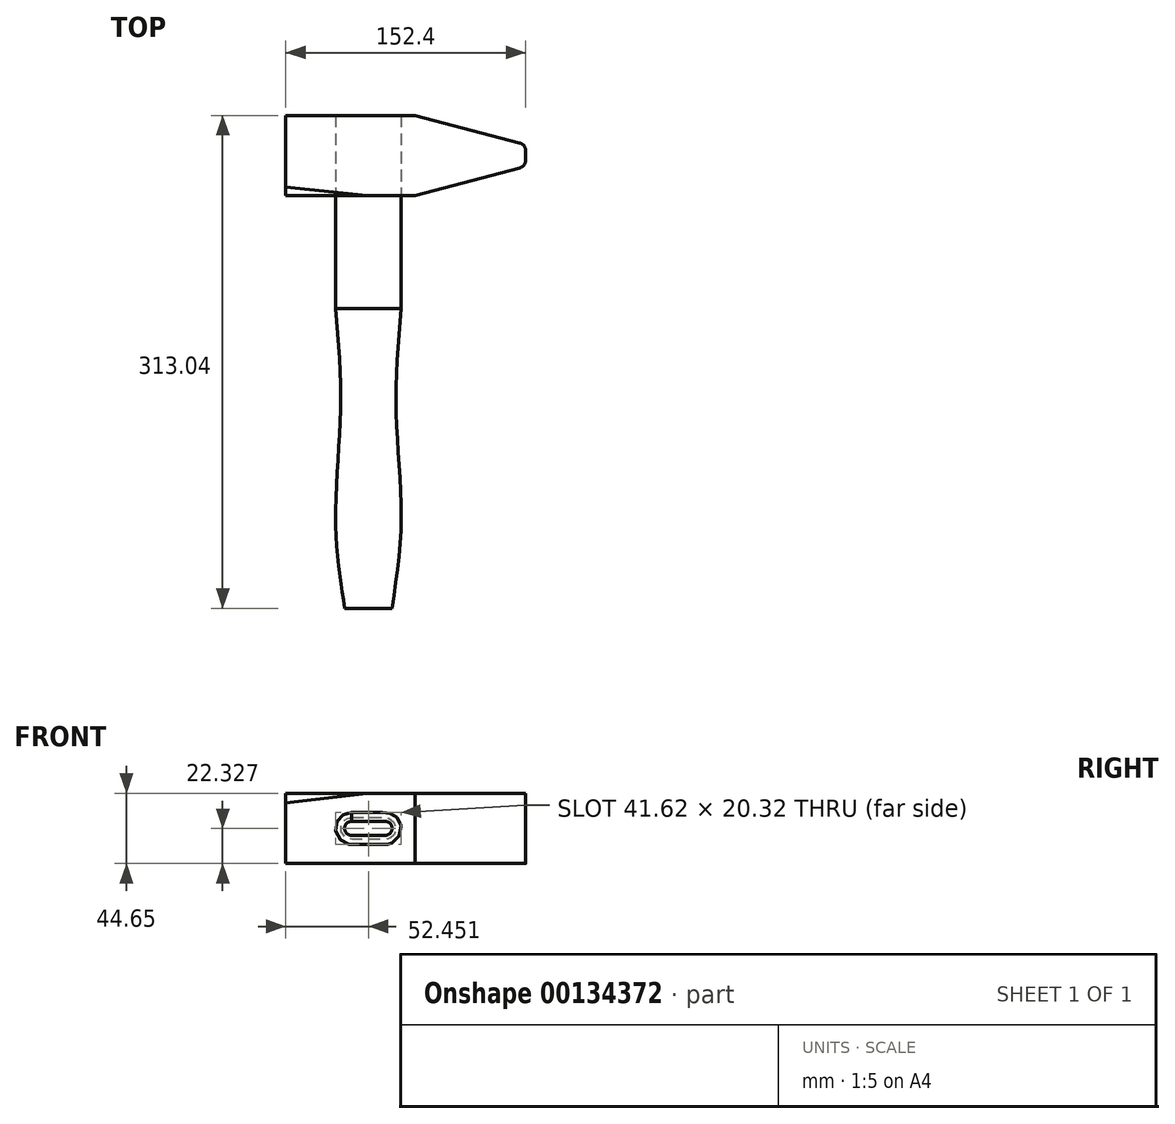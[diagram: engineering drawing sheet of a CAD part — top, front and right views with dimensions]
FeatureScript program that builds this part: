
annotation { "Feature Type Name" : "Feature", "Feature Type Description" : "" }
export const myFeature = defineFeature(function(context is Context, id is Id, definition is map)
    precondition{}
    {
        {
            var Q0;
            Q0=qCreatedBy(makeId("Top.planeOp"),FACE);
            var sketch = newSketch(context, id + "F0", { "sketchPlane" : qUnion([Q0])});
            skLineSegment(sketch, "E0", {"start": v(-120.96, 0) * mm, "end": v(179.85, 0) * mm, "construction": true});
            skLineSegment(sketch, "E1.bottom", {"start": v(-63.1, 25.4) * mm, "end": v(89.3, 25.4) * mm});
            skLineSegment(sketch, "E1.top", {"start": v(-63.1, -25.4) * mm, "end": v(89.3, -25.4) * mm});
            skLineSegment(sketch, "E1.left", {"start": v(-63.1, 25.4) * mm, "end": v(-63.1, -25.4) * mm});
            skLineSegment(sketch, "E1.right", {"start": v(89.3, 25.4) * mm, "end": v(89.3, -25.4) * mm});
            skLineSegment(sketch, "E2", {"start": v(19.1, 25.4) * mm, "end": v(89.3, 6.91) * mm});
            skLineSegment(sketch, "E3.MirrorCS", {"start": v(19.1, -25.4) * mm, "end": v(89.3, -6.91) * mm});
            skSolve(sketch);
        }
        {
            var Q0;
            {var subQ3=sQuery(id+"F0.wireOp",EDGE,"E1.left");Q0=makeQuery(id+"F0.imprint","IMPRINT",FACE,{"disambiguationData":[TD([[makeQuery(id+"F0.imprint","IMPRINT",EDGE,{"derivedFrom":subQ3}),1.0]])]});}
            extrude(context, id + "F1", {"entities" : qUnion([Q0]), "depth" : 44.65 * mm});
        }
        {
            var Q0;
            Q0=makeQuery(id+"F1.opExtrude","SWEPT_FACE",FACE,{"disambiguationData":[OSD([sQuery(id+"F0.wireOp",EDGE,"E1.top")])]});
            var sketch = newSketch(context, id + "F2", { "sketchPlane" : qUnion([Q0])});
            skLineSegment(sketch, "E4", {"start": v(-76.56, 22.33) * mm, "end": v(33.96, 22.33) * mm, "construction": true});
            skPoint(sketch, "E4.startSnap0", {"position": v(-63.1, 22.33) * mm});
            skCircle(sketch, "E5", {"center": v(-21.3, 22.33) * mm, "radius": 10.16 * mm});
            skCircle(sketch, "E6", {"center": v(0, 22.33) * mm, "radius": 10.16 * mm});
            skLineSegment(sketch, "E7", {"start": v(-21.3, 32.49) * mm, "end": v(0, 32.49) * mm});
            skLineSegment(sketch, "E8", {"start": v(-21.3, 12.17) * mm, "end": v(0, 12.17) * mm});
            skSolve(sketch);
        }
        {
            var Q0;
            {var subQ0=sQuery(id+"F2.wireOp",EDGE,"E5");var subQ1=makeQuery(id+"F2.imprint","INTERSECT",VERTEX,{"derivedFrom":[subQ0,sQuery(id+"F2.wireOp",EDGE,"E7")]});Q0=makeQuery(id+"F2.imprint","IMPRINT",FACE,{"disambiguationData":[TD([[makeQuery(id+"F2.imprint","IMPRINT",EDGE,{"disambiguationData":[TD([[subQ1,-1.0]])],"derivedFrom":subQ0}),1.0]])]});}
            var Q1;
            {var subQ0=sQuery(id+"F2.wireOp",EDGE,"E7");Q1=makeQuery(id+"F2.imprint","IMPRINT",FACE,{"disambiguationData":[TD([[makeQuery(id+"F2.imprint","IMPRINT",EDGE,{"derivedFrom":subQ0}),-1.0]])]});}
            var Q2;
            {var subQ0=sQuery(id+"F2.wireOp",EDGE,"E6");var subQ1=makeQuery(id+"F2.imprint","INTERSECT",VERTEX,{"derivedFrom":[subQ0,sQuery(id+"F2.wireOp",EDGE,"E7")]});Q2=makeQuery(id+"F2.imprint","IMPRINT",FACE,{"disambiguationData":[TD([[makeQuery(id+"F2.imprint","IMPRINT",EDGE,{"disambiguationData":[TD([[subQ1,-1.0]])],"derivedFrom":subQ0}),1.0]])]});}
            extrude(context, id + "F3", {"entities" : qUnion([Q0, Q1, Q2]), "operationType" : NewBodyOperationType.REMOVE, "endBound" : BoundingType.THROUGH_ALL, "oppositeDirection" : true, "depth" : 32.32 * mm});
        }
        {
            var Q0;
            Q0=makeQuery(id+"F1.opExtrude","CAP_VERTEX",VERTEX,{"disambiguationData":[OSD([sQuery(id+"F0.wireOp",EDGE,"E1.bottom"),sQuery(id+"F0.wireOp",EDGE,"E1.left")])],"isStart":true});
            var Q1;
            Q1=makeQuery(id+"F1.opExtrude","CAP_VERTEX",VERTEX,{"disambiguationData":[OSD([sQuery(id+"F0.wireOp",EDGE,"E1.top"),sQuery(id+"F0.wireOp",EDGE,"E1.left")])],"isStart":false});
            var Q2;
            Q2=makeQuery(id+"F1.opExtrude","CAP_VERTEX",VERTEX,{"disambiguationData":[OSD([sQuery(id+"F0.wireOp",EDGE,"E1.top"),sQuery(id+"F0.wireOp",EDGE,"E3.MirrorCS")])],"isStart":false});
            cPlane(context, id + "F4", {"entities" : qUnion([Q0, Q1, Q2]), "cplaneType" : CPlaneType.THREE_POINT, "offset" : 25.4 * mm, "width" : 152.4 * mm, "height" : 152.4 * mm});
        }
        {
            var Q0;
            Q0=qCreatedBy(id+"F4.planeOp",FACE);
            var sketch = newSketch(context, id + "F5", { "sketchPlane" : qUnion([Q0])});
            skLineSegment(sketch, "E9", {"start": v(-2, 49.27) * mm, "end": v(-75.34, 43.64) * mm});
            skLineSegment(sketch, "E10", {"start": v(-75.34, 43.64) * mm, "end": v(-75.34, 57.96) * mm});
            skLineSegment(sketch, "E11", {"start": v(-75.34, 57.96) * mm, "end": v(-2, 49.27) * mm});
            skSolve(sketch);
        }
        {
            var Q0;
            Q0=makeQuery(id+"F5.imprint","IMPRINT",FACE,{"disambiguationData":[TD([[makeQuery(id+"F5.imprint","IMPRINT",EDGE,{"derivedFrom":sQuery(id+"F5.wireOp",EDGE,"E9")}),-1.0]])]});
            extrude(context, id + "F6", {"entities" : qUnion([Q0]), "operationType" : NewBodyOperationType.REMOVE, "oppositeDirection" : true, "depth" : 25.4 * mm, "hasSecondDirection" : true, "secondDirectionOppositeDirection" : false, "secondDirectionDepth" : 25.4 * mm});
        }
        {
            var Q0;
            Q0=makeQuery(id+"F1.opExtrude","SWEPT_FACE",FACE,{"disambiguationData":[OSD([sQuery(id+"F0.wireOp",EDGE,"E1.top")])]});
            var Q1;
            Q1=makeQuery(id+"F1.opExtrude","SWEPT_FACE",FACE,{"disambiguationData":[OSD([sQuery(id+"F0.wireOp",EDGE,"E1.bottom")])]});
            cPlane(context, id + "F7", {"entities" : qUnion([Q0, Q1]), "cplaneType" : CPlaneType.MID_PLANE, "offset" : 25.4 * mm, "width" : 152.4 * mm, "height" : 152.4 * mm});
        }
        {
            var Q0;
            Q0=makeQuery(id+"F1.opExtrude","CAP_FACE",FACE,{"disambiguationData":[OSD([sQuery(id+"F0.wireOp",EDGE,"E1.bottom"),sQuery(id+"F0.wireOp",EDGE,"E1.top"),sQuery(id+"F0.wireOp",EDGE,"E1.left"),sQuery(id+"F0.wireOp",EDGE,"E1.right"),sQuery(id+"F0.wireOp",EDGE,"E2"),sQuery(id+"F0.wireOp",EDGE,"E3.MirrorCS")])],"isStart":false});
            var Q1;
            Q1=makeQuery(id+"F1.opExtrude","CAP_FACE",FACE,{"disambiguationData":[OSD([sQuery(id+"F0.wireOp",EDGE,"E1.bottom"),sQuery(id+"F0.wireOp",EDGE,"E1.top"),sQuery(id+"F0.wireOp",EDGE,"E1.left"),sQuery(id+"F0.wireOp",EDGE,"E1.right"),sQuery(id+"F0.wireOp",EDGE,"E2"),sQuery(id+"F0.wireOp",EDGE,"E3.MirrorCS")])],"isStart":true});
            cPlane(context, id + "F8", {"entities" : qUnion([Q0, Q1]), "cplaneType" : CPlaneType.MID_PLANE, "offset" : 25.4 * mm, "width" : 152.4 * mm, "height" : 152.4 * mm});
        }
        {
            var Q0;
            Q0=makeQuery(id+"F1.opExtrude","SWEPT_EDGE",EDGE,{"disambiguationData":[OSD([sQuery(id+"F0.wireOp",EDGE,"E1.right"),sQuery(id+"F0.wireOp",EDGE,"E3.MirrorCS")])]});
            var Q1;
            Q1=makeQuery(id+"F1.opExtrude","SWEPT_EDGE",EDGE,{"disambiguationData":[OSD([sQuery(id+"F0.wireOp",EDGE,"E1.right"),sQuery(id+"F0.wireOp",EDGE,"E2")])]});
            fillet(context, id + "F9", {"entities" : qUnion([Q0, Q1]), "radius" : 5.08 * mm, "tangentPropagation" : true, "allowEdgeOverflow" : false});
        }
        {
            var Q0;
            Q0=makeQuery(id+"F1.opExtrude","SWEPT_FACE",FACE,{"disambiguationData":[OSD([sQuery(id+"F0.wireOp",EDGE,"E1.top")])]});
            var sketch = newSketch(context, id + "F10", { "sketchPlane" : qUnion([Q0])});
            skLineSegment(sketch, "E12.0", {"start": v(-21.3, 32.49) * mm, "end": v(0, 32.49) * mm});
            skArc(sketch, "E13.0", {"start": v(-21.3, 32.49) * mm, "mid": v(-31.46, 22.33) * mm, "end": v(-21.3, 12.17) * mm});
            skLineSegment(sketch, "E14.0", {"start": v(-21.3, 12.17) * mm, "end": v(0, 12.17) * mm});
            skArc(sketch, "E15.0", {"start": v(0, 12.17) * mm, "mid": v(10.16, 22.33) * mm, "end": v(0, 32.49) * mm});
            skLineSegment(sketch, "E16.0", {"start": v(-21.3, 32.36) * mm, "end": v(0, 32.36) * mm});
            skArc(sketch, "E16.1", {"start": v(-21.3, 32.36) * mm, "mid": v(-31.33, 22.33) * mm, "end": v(-21.3, 12.3) * mm});
            skLineSegment(sketch, "E16.2", {"start": v(-21.3, 12.3) * mm, "end": v(0, 12.3) * mm});
            skArc(sketch, "E16.3", {"start": v(0, 12.3) * mm, "mid": v(10.03, 22.33) * mm, "end": v(0, 32.36) * mm});
            skSolve(sketch);
        }
        {
            var Q0;
            Q0=makeQuery(id+"F10.imprint","IMPRINT",FACE,{"disambiguationData":[TD([[makeQuery(id+"F10.imprint","IMPRINT",EDGE,{"derivedFrom":sQuery(id+"F10.wireOp",EDGE,"E16.0")}),-1.0]])]});
            var Q1;
            Q1=makeQuery(id+"F1.opExtrude","SWEPT_FACE",FACE,{"disambiguationData":[OSD([sQuery(id+"F0.wireOp",EDGE,"E1.bottom")])]});
            extrude(context, id + "F11", {"entities" : qUnion([Q0]), "endBound" : BoundingType.UP_TO_SURFACE, "oppositeDirection" : true, "endBoundEntityFace" : qUnion([Q1]), "depth" : 49.7 * mm});
        }
        {
            var Q0;
            Q0=makeQuery(id+"F11.opExtrude","CAP_FACE",FACE,{"disambiguationData":[OSD([sQuery(id+"F10.wireOp",EDGE,"E16.0"),sQuery(id+"F10.wireOp",EDGE,"E16.1"),sQuery(id+"F10.wireOp",EDGE,"E16.2"),sQuery(id+"F10.wireOp",EDGE,"E16.3")])],"isStart":true});
            extrude(context, id + "F12", {"entities" : qUnion([Q0]), "operationType" : NewBodyOperationType.ADD, "depth" : 71.74 * mm});
        }
        {
            var Q0;
            Q0=makeQuery(id+"F12.opExtrude","CAP_FACE",FACE,{"disambiguationData":[OSD([sQuery(id+"F10.wireOp",EDGE,"E16.0"),sQuery(id+"F10.wireOp",EDGE,"E16.1"),sQuery(id+"F10.wireOp",EDGE,"E16.2"),sQuery(id+"F10.wireOp",EDGE,"E16.3")])],"isStart":false});
            cPlane(context, id + "F13", {"entities" : qUnion([Q0]), "cplaneType" : CPlaneType.OFFSET, "offset" : 63.5 * mm, "width" : 152.4 * mm, "height" : 152.4 * mm});
        }
        {
            var Q0;
            Q0=makeQuery(id+"F12.opExtrude","CAP_FACE",FACE,{"disambiguationData":[OSD([sQuery(id+"F10.wireOp",EDGE,"E16.0"),sQuery(id+"F10.wireOp",EDGE,"E16.1"),sQuery(id+"F10.wireOp",EDGE,"E16.2"),sQuery(id+"F10.wireOp",EDGE,"E16.3")])],"isStart":false});
            cPlane(context, id + "F14", {"entities" : qUnion([Q0]), "cplaneType" : CPlaneType.OFFSET, "offset" : 139.7 * mm, "width" : 152.4 * mm, "height" : 152.4 * mm});
        }
        {
            var Q0;
            Q0=qCreatedBy(id+"F14.planeOp",FACE);
            var sketch = newSketch(context, id + "F15", { "sketchPlane" : qUnion([Q0])});
            skLineSegment(sketch, "E17.0", {"start": v(-21.3, 32.36) * mm, "end": v(0, 32.36) * mm});
            skArc(sketch, "E18.0", {"start": v(-21.3, 32.36) * mm, "mid": v(-31.33, 22.33) * mm, "end": v(-21.3, 12.3) * mm});
            skLineSegment(sketch, "E19.0", {"start": v(-21.3, 12.3) * mm, "end": v(0, 12.3) * mm});
            skArc(sketch, "E20.0", {"start": v(0, 12.3) * mm, "mid": v(10.03, 22.33) * mm, "end": v(0, 32.36) * mm});
            skLineSegment(sketch, "E21.0", {"start": v(-21.3, 39.16) * mm, "end": v(0, 39.16) * mm});
            skArc(sketch, "E21.1", {"start": v(-21.3, 39.16) * mm, "mid": v(-38.14, 22.33) * mm, "end": v(-21.3, 5.49) * mm});
            skLineSegment(sketch, "E21.2", {"start": v(-21.3, 5.49) * mm, "end": v(0, 5.49) * mm});
            skArc(sketch, "E21.3", {"start": v(0, 5.49) * mm, "mid": v(16.84, 22.33) * mm, "end": v(0, 39.16) * mm});
            skSolve(sketch);
        }
        {
            var Q0;
            Q0=qCreatedBy(id+"F14.planeOp",FACE);
            cPlane(context, id + "F16", {"entities" : qUnion([Q0]), "cplaneType" : CPlaneType.OFFSET, "offset" : 50.8 * mm, "width" : 152.4 * mm, "height" : 152.4 * mm});
        }
        {
            var Q0;
            Q0=qCreatedBy(id+"F16.planeOp",FACE);
            var sketch = newSketch(context, id + "F17", { "sketchPlane" : qUnion([Q0])});
            skArc(sketch, "E22.0", {"start": v(-21.3, 32.36) * mm, "mid": v(-31.33, 22.33) * mm, "end": v(-21.3, 12.3) * mm});
            skLineSegment(sketch, "E23.0", {"start": v(-21.3, 12.3) * mm, "end": v(0, 12.3) * mm});
            skLineSegment(sketch, "E24.0", {"start": v(-21.3, 32.36) * mm, "end": v(0, 32.36) * mm});
            skArc(sketch, "E25.0", {"start": v(0, 12.3) * mm, "mid": v(10.03, 22.33) * mm, "end": v(0, 32.36) * mm});
            skArc(sketch, "E26.0", {"start": v(-21.3, 26.77) * mm, "mid": v(-25.74, 22.33) * mm, "end": v(-21.3, 17.88) * mm});
            skLineSegment(sketch, "E26.1", {"start": v(-21.3, 26.77) * mm, "end": v(0, 26.77) * mm});
            skArc(sketch, "E26.2", {"start": v(0, 17.88) * mm, "mid": v(4.44, 22.33) * mm, "end": v(0, 26.77) * mm});
            skLineSegment(sketch, "E26.3", {"start": v(-21.3, 17.88) * mm, "end": v(0, 17.88) * mm});
            skSolve(sketch);
        }
        {
            var Q0;
            Q0=qCreatedBy(id+"F13.planeOp",FACE);
            var sketch = newSketch(context, id + "F18", { "sketchPlane" : qUnion([Q0])});
            skArc(sketch, "E27.0", {"start": v(-21.3, 32.36) * mm, "mid": v(-31.33, 22.33) * mm, "end": v(-21.3, 12.3) * mm});
            skLineSegment(sketch, "E28.0", {"start": v(-21.3, 32.36) * mm, "end": v(0, 32.36) * mm});
            skLineSegment(sketch, "E29.0", {"start": v(-21.3, 12.3) * mm, "end": v(0, 12.3) * mm});
            skArc(sketch, "E30.0", {"start": v(0, 12.3) * mm, "mid": v(10.03, 22.33) * mm, "end": v(0, 32.36) * mm});
            skArc(sketch, "E31.0", {"start": v(-21.3, 29.31) * mm, "mid": v(-28.28, 22.33) * mm, "end": v(-21.3, 15.34) * mm});
            skLineSegment(sketch, "E31.1", {"start": v(-21.3, 29.31) * mm, "end": v(0, 29.31) * mm});
            skArc(sketch, "E31.2", {"start": v(0, 15.34) * mm, "mid": v(6.99, 22.33) * mm, "end": v(0, 29.31) * mm});
            skLineSegment(sketch, "E31.3", {"start": v(-21.3, 15.34) * mm, "end": v(0, 15.34) * mm});
            skSolve(sketch);
        }
        {
            var Q1;
            Q1=makeQuery(id+"F12.opExtrude","CAP_FACE",FACE,{"disambiguationData":[OSD([sQuery(id+"F10.wireOp",EDGE,"E16.0"),sQuery(id+"F10.wireOp",EDGE,"E16.1"),sQuery(id+"F10.wireOp",EDGE,"E16.2"),sQuery(id+"F10.wireOp",EDGE,"E16.3")])],"isStart":false});
            var Q2;
            Q2=makeQuery(id+"F18.imprint","IMPRINT",FACE,{"disambiguationData":[TD([[makeQuery(id+"F18.imprint","IMPRINT",EDGE,{"derivedFrom":sQuery(id+"F18.wireOp",EDGE,"E31.0")}),1.0]])]});
            var Q3;
            Q3=makeQuery(id+"F15.imprint","IMPRINT",FACE,{"disambiguationData":[TD([[makeQuery(id+"F15.imprint","IMPRINT",EDGE,{"derivedFrom":sQuery(id+"F15.wireOp",EDGE,"E17.0")}),-1.0]])]});
            var Q4;
            Q4=makeQuery(id+"F17.imprint","IMPRINT",FACE,{"disambiguationData":[TD([[makeQuery(id+"F17.imprint","IMPRINT",EDGE,{"derivedFrom":sQuery(id+"F17.wireOp",EDGE,"E26.0")}),1.0]])]});
            loft(context, id + "F19", {"operationType" : NewBodyOperationType.ADD, "sheetProfilesArray" : [{ "sheetProfileEntities" : qUnion([Q1]) }, { "sheetProfileEntities" : qUnion([Q2]) }, { "sheetProfileEntities" : qUnion([Q3]) }, { "sheetProfileEntities" : qUnion([Q4]) }]});
        }
    });
